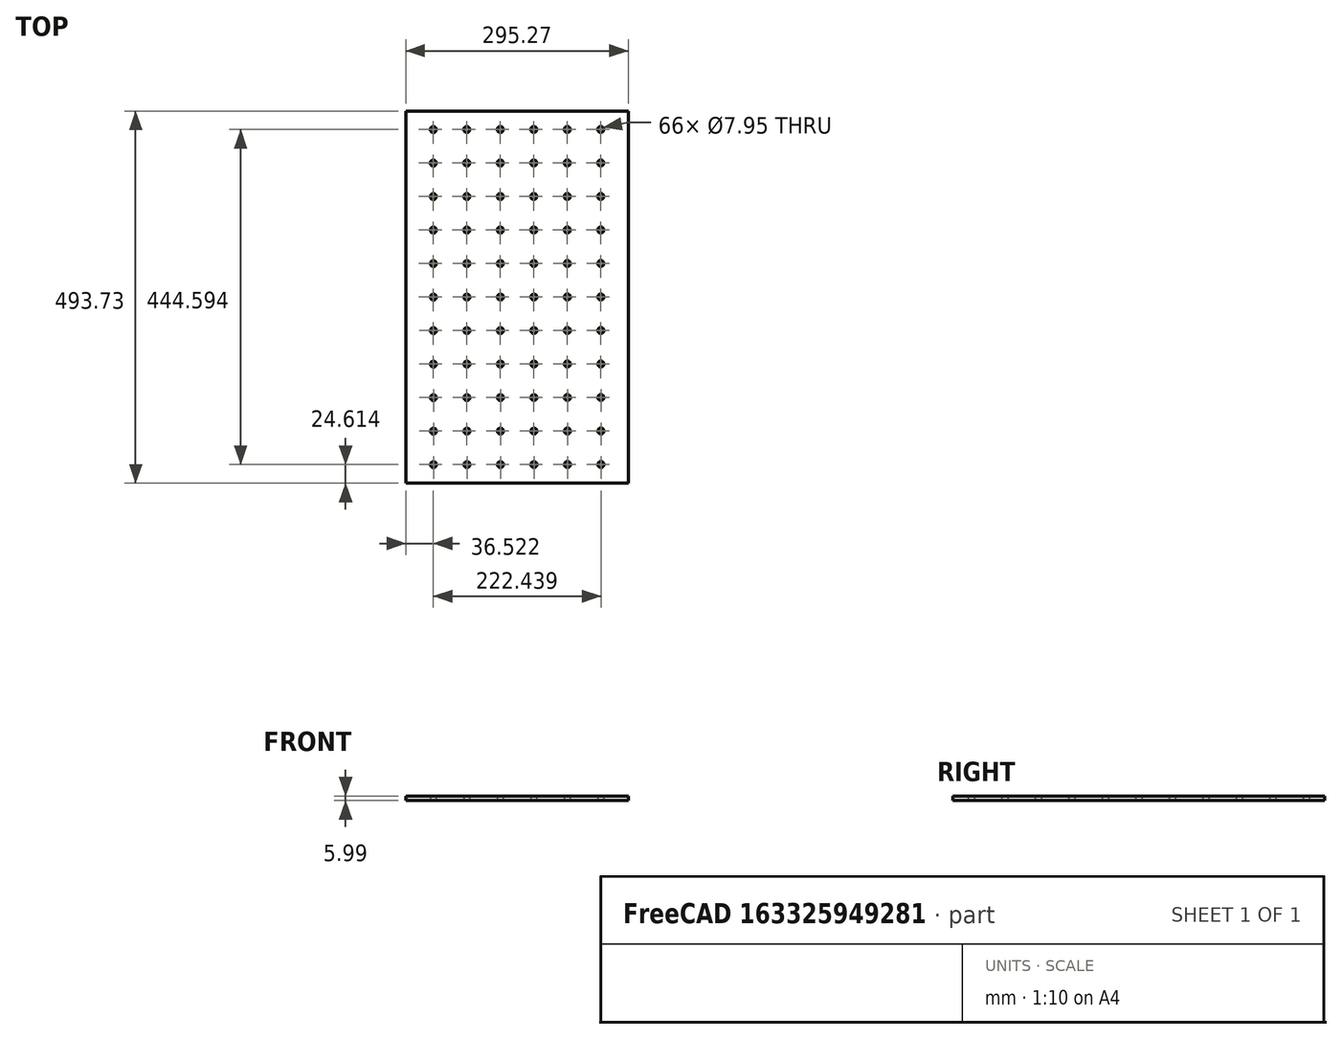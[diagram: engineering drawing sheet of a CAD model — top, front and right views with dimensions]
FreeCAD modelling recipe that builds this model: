
FCSTD DOCUMENT  (FreeCAD 0.19R24267 (Git))
Label: Up1-P2
License: All rights reserved
LicenseURL: http://en.wikipedia.org/wiki/All_rights_reserved
objects: TechDraw::DrawViewDimension×8, TechDraw::DrawViewAnnotation×3, TechDraw::DrawProjGroupItem×2, TechDraw::DrawHatch×2, Sketcher::SketchObject×1, Part::Extrusion×1, TechDraw::DrawSVGTemplate×1, TechDraw::DrawProjGroup×1, TechDraw::DrawPage×1
note: 2 computed .brp shape members not serialized (recipe doc carries the construction recipe); baked Part::Feature solids carry a one-line shape summary decoded from their .brp

FEATURE [Sketcher::SketchObject] Sketch
  FullyConstrained = false
  sketch-geometry (135):
    g0: LineSegment StartX=210.166 StartY=-388.383 StartZ=0 EndX=505.441 EndY=-388.383 EndZ=0
    g1: LineSegment StartX=505.441 StartY=-388.383 StartZ=0 EndX=505.441 EndY=-882.108 EndZ=0
    g2: LineSegment StartX=505.441 StartY=-882.108 StartZ=0 EndX=210.166 EndY=-882.108 EndZ=0
    g3: LineSegment StartX=210.166 StartY=-882.108 StartZ=0 EndX=210.166 EndY=-388.383 EndZ=0
    g4: Circle CenterX=246.692 CenterY=-412.996 CenterZ=0 NormalX=0 NormalY=0 NormalZ=1 AngleXU=0 Radius=3.9751
    g5: Circle CenterX=291.142 CenterY=-412.977 CenterZ=0 NormalX=0 NormalY=0 NormalZ=1 AngleXU=0 Radius=3.9751
    g6: LineSegment StartX=246.692 StartY=-412.996 StartZ=0 EndX=291.142 EndY=-412.977 EndZ=0
    g7: Circle CenterX=335.592 CenterY=-412.958 CenterZ=0 NormalX=0 NormalY=0 NormalZ=1 AngleXU=0 Radius=3.9751
    g8: LineSegment StartX=291.142 StartY=-412.977 StartZ=0 EndX=335.592 EndY=-412.958 EndZ=0
    g9: Circle CenterX=380.042 CenterY=-412.939 CenterZ=0 NormalX=0 NormalY=0 NormalZ=1 AngleXU=0 Radius=3.9751
    g10: LineSegment StartX=335.592 StartY=-412.958 StartZ=0 EndX=380.042 EndY=-412.939 EndZ=0
    g11: Circle CenterX=424.492 CenterY=-412.92 CenterZ=0 NormalX=0 NormalY=0 NormalZ=1 AngleXU=0 Radius=3.9751
    g12: LineSegment StartX=380.042 StartY=-412.939 StartZ=0 EndX=424.492 EndY=-412.92 EndZ=0
    g13: Circle CenterX=468.942 CenterY=-412.901 CenterZ=0 NormalX=0 NormalY=0 NormalZ=1 AngleXU=0 Radius=3.9751
    g14: LineSegment StartX=424.492 StartY=-412.92 StartZ=0 EndX=468.942 EndY=-412.901 EndZ=0
    g15: Circle CenterX=246.71 CenterY=-457.446 CenterZ=0 NormalX=0 NormalY=0 NormalZ=1 AngleXU=0 Radius=3.9751
    g16: LineSegment StartX=246.692 StartY=-412.996 StartZ=0 EndX=246.71 EndY=-457.446 EndZ=0
    g17: Circle CenterX=291.16 CenterY=-457.427 CenterZ=0 NormalX=0 NormalY=0 NormalZ=1 AngleXU=0 Radius=3.9751
    g18: LineSegment StartX=246.71 StartY=-457.446 StartZ=0 EndX=291.16 EndY=-457.427 EndZ=0
    g19: Circle CenterX=335.61 CenterY=-457.408 CenterZ=0 NormalX=0 NormalY=0 NormalZ=1 AngleXU=0 Radius=3.9751
    g20: LineSegment StartX=291.16 StartY=-457.427 StartZ=0 EndX=335.61 EndY=-457.408 EndZ=0
    g21: Circle CenterX=380.06 CenterY=-457.389 CenterZ=0 NormalX=0 NormalY=0 NormalZ=1 AngleXU=0 Radius=3.9751
    g22: LineSegment StartX=335.61 StartY=-457.408 StartZ=0 EndX=380.06 EndY=-457.389 EndZ=0
    g23: Circle CenterX=424.51 CenterY=-457.37 CenterZ=0 NormalX=0 NormalY=0 NormalZ=1 AngleXU=0 Radius=3.9751
    g24: LineSegment StartX=380.06 StartY=-457.389 StartZ=0 EndX=424.51 EndY=-457.37 EndZ=0
    g25: Circle CenterX=468.96 CenterY=-457.351 CenterZ=0 NormalX=0 NormalY=0 NormalZ=1 AngleXU=0 Radius=3.9751
    g26: LineSegment StartX=424.51 StartY=-457.37 StartZ=0 EndX=468.96 EndY=-457.351 EndZ=0
    g27: Circle CenterX=246.729 CenterY=-501.896 CenterZ=0 NormalX=0 NormalY=0 NormalZ=1 AngleXU=0 Radius=3.9751
    g28: LineSegment StartX=246.71 StartY=-457.446 StartZ=0 EndX=246.729 EndY=-501.896 EndZ=0
    g29: Circle CenterX=291.179 CenterY=-501.877 CenterZ=0 NormalX=0 NormalY=0 NormalZ=1 AngleXU=0 Radius=3.9751
    g30: LineSegment StartX=246.729 StartY=-501.896 StartZ=0 EndX=291.179 EndY=-501.877 EndZ=0
    g31: Circle CenterX=335.629 CenterY=-501.858 CenterZ=0 NormalX=0 NormalY=0 NormalZ=1 AngleXU=0 Radius=3.9751
    g32: LineSegment StartX=291.179 StartY=-501.877 StartZ=0 EndX=335.629 EndY=-501.858 EndZ=0
    g33: Circle CenterX=380.079 CenterY=-501.839 CenterZ=0 NormalX=0 NormalY=0 NormalZ=1 AngleXU=0 Radius=3.9751
    g34: LineSegment StartX=335.629 StartY=-501.858 StartZ=0 EndX=380.079 EndY=-501.839 EndZ=0
    g35: Circle CenterX=424.529 CenterY=-501.82 CenterZ=0 NormalX=0 NormalY=0 NormalZ=1 AngleXU=0 Radius=3.9751
    g36: LineSegment StartX=380.079 StartY=-501.839 StartZ=0 EndX=424.529 EndY=-501.82 EndZ=0
    g37: Circle CenterX=468.979 CenterY=-501.801 CenterZ=0 NormalX=0 NormalY=0 NormalZ=1 AngleXU=0 Radius=3.9751
    g38: LineSegment StartX=424.529 StartY=-501.82 StartZ=0 EndX=468.979 EndY=-501.801 EndZ=0
    g39: Circle CenterX=246.748 CenterY=-546.346 CenterZ=0 NormalX=0 NormalY=0 NormalZ=1 AngleXU=0 Radius=3.9751
    g40: LineSegment StartX=246.729 StartY=-501.896 StartZ=0 EndX=246.748 EndY=-546.346 EndZ=0
    g41: Circle CenterX=291.198 CenterY=-546.327 CenterZ=0 NormalX=0 NormalY=0 NormalZ=1 AngleXU=0 Radius=3.9751
    g42: LineSegment StartX=246.748 StartY=-546.346 StartZ=0 EndX=291.198 EndY=-546.327 EndZ=0
    g43: Circle CenterX=335.648 CenterY=-546.308 CenterZ=0 NormalX=0 NormalY=0 NormalZ=1 AngleXU=0 Radius=3.9751
    g44: LineSegment StartX=291.198 StartY=-546.327 StartZ=0 EndX=335.648 EndY=-546.308 EndZ=0
    g45: Circle CenterX=380.098 CenterY=-546.289 CenterZ=0 NormalX=0 NormalY=0 NormalZ=1 AngleXU=0 Radius=3.9751
    g46: LineSegment StartX=335.648 StartY=-546.308 StartZ=0 EndX=380.098 EndY=-546.289 EndZ=0
    g47: Circle CenterX=424.548 CenterY=-546.27 CenterZ=0 NormalX=0 NormalY=0 NormalZ=1 AngleXU=0 Radius=3.9751
    g48: LineSegment StartX=380.098 StartY=-546.289 StartZ=0 EndX=424.548 EndY=-546.27 EndZ=0
    g49: Circle CenterX=468.998 CenterY=-546.251 CenterZ=0 NormalX=0 NormalY=0 NormalZ=1 AngleXU=0 Radius=3.9751
    g50: LineSegment StartX=424.548 StartY=-546.27 StartZ=0 EndX=468.998 EndY=-546.251 EndZ=0
    g51: Circle CenterX=246.767 CenterY=-590.796 CenterZ=0 NormalX=0 NormalY=0 NormalZ=1 AngleXU=0 Radius=3.9751
    g52: LineSegment StartX=246.748 StartY=-546.346 StartZ=0 EndX=246.767 EndY=-590.796 EndZ=0
    g53: Circle CenterX=291.217 CenterY=-590.777 CenterZ=0 NormalX=0 NormalY=0 NormalZ=1 AngleXU=0 Radius=3.9751
    g54: LineSegment StartX=246.767 StartY=-590.796 StartZ=0 EndX=291.217 EndY=-590.777 EndZ=0
    g55: Circle CenterX=335.667 CenterY=-590.758 CenterZ=0 NormalX=0 NormalY=0 NormalZ=1 AngleXU=0 Radius=3.9751
    g56: LineSegment StartX=291.217 StartY=-590.777 StartZ=0 EndX=335.667 EndY=-590.758 EndZ=0
    g57: Circle CenterX=380.117 CenterY=-590.739 CenterZ=0 NormalX=0 NormalY=0 NormalZ=1 AngleXU=0 Radius=3.9751
    g58: LineSegment StartX=335.667 StartY=-590.758 StartZ=0 EndX=380.117 EndY=-590.739 EndZ=0
    g59: Circle CenterX=424.567 CenterY=-590.72 CenterZ=0 NormalX=0 NormalY=0 NormalZ=1 AngleXU=0 Radius=3.9751
    g60: LineSegment StartX=380.117 StartY=-590.739 StartZ=0 EndX=424.567 EndY=-590.72 EndZ=0
    g61: Circle CenterX=469.017 CenterY=-590.701 CenterZ=0 NormalX=0 NormalY=0 NormalZ=1 AngleXU=0 Radius=3.9751
    g62: LineSegment StartX=424.567 StartY=-590.72 StartZ=0 EndX=469.017 EndY=-590.701 EndZ=0
    g63: Circle CenterX=246.786 CenterY=-635.246 CenterZ=0 NormalX=0 NormalY=0 NormalZ=1 AngleXU=0 Radius=3.9751
    g64: LineSegment StartX=246.767 StartY=-590.796 StartZ=0 EndX=246.786 EndY=-635.246 EndZ=0
    g65: Circle CenterX=291.236 CenterY=-635.227 CenterZ=0 NormalX=0 NormalY=0 NormalZ=1 AngleXU=0 Radius=3.9751
    g66: LineSegment StartX=246.786 StartY=-635.246 StartZ=0 EndX=291.236 EndY=-635.227 EndZ=0
    g67: Circle CenterX=335.686 CenterY=-635.208 CenterZ=0 NormalX=0 NormalY=0 NormalZ=1 AngleXU=0 Radius=3.9751
    g68: LineSegment StartX=291.236 StartY=-635.227 StartZ=0 EndX=335.686 EndY=-635.208 EndZ=0
    g69: Circle CenterX=380.136 CenterY=-635.189 CenterZ=0 NormalX=0 NormalY=0 NormalZ=1 AngleXU=0 Radius=3.9751
    g70: LineSegment StartX=335.686 StartY=-635.208 StartZ=0 EndX=380.136 EndY=-635.189 EndZ=0
    g71: Circle CenterX=424.586 CenterY=-635.17 CenterZ=0 NormalX=0 NormalY=0 NormalZ=1 AngleXU=0 Radius=3.9751
    g72: LineSegment StartX=380.136 StartY=-635.189 StartZ=0 EndX=424.586 EndY=-635.17 EndZ=0
    g73: Circle CenterX=469.036 CenterY=-635.151 CenterZ=0 NormalX=0 NormalY=0 NormalZ=1 AngleXU=0 Radius=3.9751
    g74: LineSegment StartX=424.586 StartY=-635.17 StartZ=0 EndX=469.036 EndY=-635.151 EndZ=0
    g75: Circle CenterX=246.805 CenterY=-679.696 CenterZ=0 NormalX=0 NormalY=0 NormalZ=1 AngleXU=0 Radius=3.9751
    g76: LineSegment StartX=246.786 StartY=-635.246 StartZ=0 EndX=246.805 EndY=-679.696 EndZ=0
    g77: Circle CenterX=291.255 CenterY=-679.677 CenterZ=0 NormalX=0 NormalY=0 NormalZ=1 AngleXU=0 Radius=3.9751
    g78: LineSegment StartX=246.805 StartY=-679.696 StartZ=0 EndX=291.255 EndY=-679.677 EndZ=0
    g79: Circle CenterX=335.705 CenterY=-679.658 CenterZ=0 NormalX=0 NormalY=0 NormalZ=1 AngleXU=0 Radius=3.9751
    g80: LineSegment StartX=291.255 StartY=-679.677 StartZ=0 EndX=335.705 EndY=-679.658 EndZ=0
    g81: Circle CenterX=380.155 CenterY=-679.639 CenterZ=0 NormalX=0 NormalY=0 NormalZ=1 AngleXU=0 Radius=3.9751
    g82: LineSegment StartX=335.705 StartY=-679.658 StartZ=0 EndX=380.155 EndY=-679.639 EndZ=0
    g83: Circle CenterX=424.605 CenterY=-679.62 CenterZ=0 NormalX=0 NormalY=0 NormalZ=1 AngleXU=0 Radius=3.9751
    g84: LineSegment StartX=380.155 StartY=-679.639 StartZ=0 EndX=424.605 EndY=-679.62 EndZ=0
    g85: Circle CenterX=469.055 CenterY=-679.601 CenterZ=0 NormalX=0 NormalY=0 NormalZ=1 AngleXU=0 Radius=3.9751
    g86: LineSegment StartX=424.605 StartY=-679.62 StartZ=0 EndX=469.055 EndY=-679.601 EndZ=0
    g87: Circle CenterX=246.824 CenterY=-724.146 CenterZ=0 NormalX=0 NormalY=0 NormalZ=1 AngleXU=0 Radius=3.9751
    g88: LineSegment StartX=246.805 StartY=-679.696 StartZ=0 EndX=246.824 EndY=-724.146 EndZ=0
    g89: Circle CenterX=291.274 CenterY=-724.127 CenterZ=0 NormalX=0 NormalY=0 NormalZ=1 AngleXU=0 Radius=3.9751
    g90: LineSegment StartX=246.824 StartY=-724.146 StartZ=0 EndX=291.274 EndY=-724.127 EndZ=0
    g91: Circle CenterX=335.724 CenterY=-724.108 CenterZ=0 NormalX=0 NormalY=0 NormalZ=1 AngleXU=0 Radius=3.9751
    g92: LineSegment StartX=291.274 StartY=-724.127 StartZ=0 EndX=335.724 EndY=-724.108 EndZ=0
    g93: Circle CenterX=380.174 CenterY=-724.089 CenterZ=0 NormalX=0 NormalY=0 NormalZ=1 AngleXU=0 Radius=3.9751
    g94: LineSegment StartX=335.724 StartY=-724.108 StartZ=0 EndX=380.174 EndY=-724.089 EndZ=0
    g95: Circle CenterX=424.624 CenterY=-724.07 CenterZ=0 NormalX=0 NormalY=0 NormalZ=1 AngleXU=0 Radius=3.9751
    g96: LineSegment StartX=380.174 StartY=-724.089 StartZ=0 EndX=424.624 EndY=-724.07 EndZ=0
    g97: Circle CenterX=469.074 CenterY=-724.051 CenterZ=0 NormalX=0 NormalY=0 NormalZ=1 AngleXU=0 Radius=3.9751
    g98: LineSegment StartX=424.624 StartY=-724.07 StartZ=0 EndX=469.074 EndY=-724.051 EndZ=0
    g99: Circle CenterX=246.843 CenterY=-768.596 CenterZ=0 NormalX=0 NormalY=0 NormalZ=1 AngleXU=0 Radius=3.9751
    g100: LineSegment StartX=246.824 StartY=-724.146 StartZ=0 EndX=246.843 EndY=-768.596 EndZ=0
    g101: Circle CenterX=291.293 CenterY=-768.577 CenterZ=0 NormalX=0 NormalY=0 NormalZ=1 AngleXU=0 Radius=3.9751
    g102: LineSegment StartX=246.843 StartY=-768.596 StartZ=0 EndX=291.293 EndY=-768.577 EndZ=0
    g103: Circle CenterX=335.743 CenterY=-768.558 CenterZ=0 NormalX=0 NormalY=0 NormalZ=1 AngleXU=0 Radius=3.9751
    g104: LineSegment StartX=291.293 StartY=-768.577 StartZ=0 EndX=335.743 EndY=-768.558 EndZ=0
    g105: Circle CenterX=380.193 CenterY=-768.539 CenterZ=0 NormalX=0 NormalY=0 NormalZ=1 AngleXU=0 Radius=3.9751
    g106: LineSegment StartX=335.743 StartY=-768.558 StartZ=0 EndX=380.193 EndY=-768.539 EndZ=0
    g107: Circle CenterX=424.643 CenterY=-768.52 CenterZ=0 NormalX=0 NormalY=0 NormalZ=1 AngleXU=0 Radius=3.9751
    g108: LineSegment StartX=380.193 StartY=-768.539 StartZ=0 EndX=424.643 EndY=-768.52 EndZ=0
    g109: Circle CenterX=469.093 CenterY=-768.501 CenterZ=0 NormalX=0 NormalY=0 NormalZ=1 AngleXU=0 Radius=3.9751
    g110: LineSegment StartX=424.643 StartY=-768.52 StartZ=0 EndX=469.093 EndY=-768.501 EndZ=0
    g111: Circle CenterX=246.862 CenterY=-813.046 CenterZ=0 NormalX=0 NormalY=0 NormalZ=1 AngleXU=0 Radius=3.9751
    g112: LineSegment StartX=246.843 StartY=-768.596 StartZ=0 EndX=246.862 EndY=-813.046 EndZ=0
    g113: Circle CenterX=291.312 CenterY=-813.027 CenterZ=0 NormalX=0 NormalY=0 NormalZ=1 AngleXU=0 Radius=3.9751
    g114: LineSegment StartX=246.862 StartY=-813.046 StartZ=0 EndX=291.312 EndY=-813.027 EndZ=0
    g115: Circle CenterX=335.762 CenterY=-813.008 CenterZ=0 NormalX=0 NormalY=0 NormalZ=1 AngleXU=0 Radius=3.9751
    g116: LineSegment StartX=291.312 StartY=-813.027 StartZ=0 EndX=335.762 EndY=-813.008 EndZ=0
    g117: Circle CenterX=380.212 CenterY=-812.989 CenterZ=0 NormalX=0 NormalY=0 NormalZ=1 AngleXU=0 Radius=3.9751
    g118: LineSegment StartX=335.762 StartY=-813.008 StartZ=0 EndX=380.212 EndY=-812.989 EndZ=0
    g119: Circle CenterX=424.662 CenterY=-812.97 CenterZ=0 NormalX=0 NormalY=0 NormalZ=1 AngleXU=0 Radius=3.9751
    g120: LineSegment StartX=380.212 StartY=-812.989 StartZ=0 EndX=424.662 EndY=-812.97 EndZ=0
    g121: Circle CenterX=469.112 CenterY=-812.951 CenterZ=0 NormalX=0 NormalY=0 NormalZ=1 AngleXU=0 Radius=3.9751
    g122: LineSegment StartX=424.662 StartY=-812.97 StartZ=0 EndX=469.112 EndY=-812.951 EndZ=0
    g123: Circle CenterX=246.88 CenterY=-857.496 CenterZ=0 NormalX=0 NormalY=0 NormalZ=1 AngleXU=0 Radius=3.9751
    g124: LineSegment StartX=246.862 StartY=-813.046 StartZ=0 EndX=246.88 EndY=-857.496 EndZ=0
    g125: Circle CenterX=291.33 CenterY=-857.477 CenterZ=0 NormalX=0 NormalY=0 NormalZ=1 AngleXU=0 Radius=3.9751
    g126: LineSegment StartX=246.88 StartY=-857.496 StartZ=0 EndX=291.33 EndY=-857.477 EndZ=0
    g127: Circle CenterX=335.78 CenterY=-857.458 CenterZ=0 NormalX=0 NormalY=0 NormalZ=1 AngleXU=0 Radius=3.9751
    g128: LineSegment StartX=291.33 StartY=-857.477 StartZ=0 EndX=335.78 EndY=-857.458 EndZ=0
    g129: Circle CenterX=380.23 CenterY=-857.439 CenterZ=0 NormalX=0 NormalY=0 NormalZ=1 AngleXU=0 Radius=3.9751
    g130: LineSegment StartX=335.78 StartY=-857.458 StartZ=0 EndX=380.23 EndY=-857.439 EndZ=0
    g131: Circle CenterX=424.68 CenterY=-857.42 CenterZ=0 NormalX=0 NormalY=0 NormalZ=1 AngleXU=0 Radius=3.9751
    g132: LineSegment StartX=380.23 StartY=-857.439 StartZ=0 EndX=424.68 EndY=-857.42 EndZ=0
    g133: Circle CenterX=469.13 CenterY=-857.401 CenterZ=0 NormalX=0 NormalY=0 NormalZ=1 AngleXU=0 Radius=3.9751
    g134: LineSegment StartX=424.68 StartY=-857.42 StartZ=0 EndX=469.13 EndY=-857.401 EndZ=0
  constraints (338):
    c: Coincident(g0,g1)
    c: Coincident(g1,g2)
    c: Coincident(g2,g3)
    c: Coincident(g3,g0)
    c: Horizontal(g0)
    c: Horizontal(g2)
    c: Vertical(g1)
    c: Vertical(g3)
    c: Distance(g0,g1) = 295.275
    c: Distance(g0,g2) = 493.725
    c: Diameter(g4) = 7.9502
    c: Distance(g4,g3) = 36.5252
    c: Distance(g4,g0) = 24.6126
    c: Diameter(g5) = 7.9502
    c: Coincident(g4,g6)
    c: Coincident(g5,g6)
    c: Distance(g6) = 44.45
    c: Angle(g6) = 0.00042473
    c: Diameter(g7) = 7.9502
    c: Coincident(g5,g8)
    c: Coincident(g7,g8)
    c: Equal(g6,g8)
    c: Parallel(g8,g6)
    c: Diameter(g9) = 7.9502
    c: Coincident(g7,g10)
    c: Coincident(g9,g10)
    c: Equal(g6,g10)
    c: Parallel(g10,g6)
    c: Diameter(g11) = 7.9502
    c: Coincident(g9,g12)
    c: Coincident(g11,g12)
    c: Equal(g6,g12)
    c: Parallel(g12,g6)
    c: Diameter(g13) = 7.9502
    c: Coincident(g11,g14)
    c: Coincident(g13,g14)
    c: Equal(g6,g14)
    c: Parallel(g14,g6)
    c: Diameter(g15) = 7.9502
    c: Coincident(g4,g16)
    c: Coincident(g15,g16)
    c: Equal(g16,g6)
    c: Perpendicular(g16,g6)
    c: Diameter(g17) = 7.9502
    c: Coincident(g15,g18)
    c: Coincident(g17,g18)
    c: Equal(g6,g18)
    c: Parallel(g18,g6)
    c: Diameter(g19) = 7.9502
    c: Coincident(g17,g20)
    c: Coincident(g19,g20)
    c: Equal(g6,g20)
    c: Parallel(g20,g6)
    c: Diameter(g21) = 7.9502
    c: Coincident(g19,g22)
    c: Coincident(g21,g22)
    c: Equal(g6,g22)
    c: Parallel(g22,g6)
    c: Diameter(g23) = 7.9502
    c: Coincident(g21,g24)
    c: Coincident(g23,g24)
    c: Equal(g6,g24)
    c: Parallel(g24,g6)
    c: Diameter(g25) = 7.9502
    c: Coincident(g23,g26)
    c: Coincident(g25,g26)
    c: Equal(g6,g26)
    c: Parallel(g26,g6)
    c: Diameter(g27) = 7.9502
    c: Coincident(g15,g28)
    c: Coincident(g27,g28)
    c: Equal(g16,g28)
    c: Perpendicular(g28,g6)
    c: Diameter(g29) = 7.9502
    c: Coincident(g27,g30)
    c: Coincident(g29,g30)
    c: Equal(g6,g30)
    c: Parallel(g30,g6)
    c: Diameter(g31) = 7.9502
    c: Coincident(g29,g32)
    c: Coincident(g31,g32)
    c: Equal(g6,g32)
    c: Parallel(g32,g6)
    c: Diameter(g33) = 7.9502
    c: Coincident(g31,g34)
    c: Coincident(g33,g34)
    c: Equal(g6,g34)
    c: Parallel(g34,g6)
    c: Diameter(g35) = 7.9502
    c: Coincident(g33,g36)
    c: Coincident(g35,g36)
    c: Equal(g6,g36)
    c: Parallel(g36,g6)
    c: Diameter(g37) = 7.9502
    c: Coincident(g35,g38)
    c: Coincident(g37,g38)
    c: Equal(g6,g38)
    c: Parallel(g38,g6)
    c: Diameter(g39) = 7.9502
    c: Coincident(g27,g40)
    c: Coincident(g39,g40)
    c: Equal(g16,g40)
    c: Perpendicular(g40,g6)
    c: Diameter(g41) = 7.9502
    c: Coincident(g39,g42)
    c: Coincident(g41,g42)
    c: Equal(g6,g42)
    c: Parallel(g42,g6)
    c: Diameter(g43) = 7.9502
    c: Coincident(g41,g44)
    c: Coincident(g43,g44)
    c: Equal(g6,g44)
    c: Parallel(g44,g6)
    c: Diameter(g45) = 7.9502
    c: Coincident(g43,g46)
    c: Coincident(g45,g46)
    c: Equal(g6,g46)
    c: Parallel(g46,g6)
    c: Diameter(g47) = 7.9502
    c: Coincident(g45,g48)
    c: Coincident(g47,g48)
    c: Equal(g6,g48)
    c: Parallel(g48,g6)
    c: Diameter(g49) = 7.9502
    c: Coincident(g47,g50)
    c: Coincident(g49,g50)
    c: Equal(g6,g50)
    c: Parallel(g50,g6)
    c: Diameter(g51) = 7.9502
    c: Coincident(g39,g52)
    c: Coincident(g51,g52)
    c: Equal(g16,g52)
    c: Perpendicular(g52,g6)
    c: Diameter(g53) = 7.9502
    c: Coincident(g51,g54)
    c: Coincident(g53,g54)
    c: Equal(g6,g54)
    c: Parallel(g54,g6)
    c: Diameter(g55) = 7.9502
    c: Coincident(g53,g56)
    c: Coincident(g55,g56)
    c: Equal(g6,g56)
    c: Parallel(g56,g6)
    c: Diameter(g57) = 7.9502
    c: Coincident(g55,g58)
    c: Coincident(g57,g58)
    c: Equal(g6,g58)
    c: Parallel(g58,g6)
    c: Diameter(g59) = 7.9502
    c: Coincident(g57,g60)
    c: Coincident(g59,g60)
    c: Equal(g6,g60)
    c: Parallel(g60,g6)
    c: Diameter(g61) = 7.9502
    c: Coincident(g59,g62)
    c: Coincident(g61,g62)
    c: Equal(g6,g62)
    c: Parallel(g62,g6)
    c: Diameter(g63) = 7.9502
    c: Coincident(g51,g64)
    c: Coincident(g63,g64)
    c: Equal(g16,g64)
    c: Perpendicular(g64,g6)
    c: Diameter(g65) = 7.9502
    c: Coincident(g63,g66)
    c: Coincident(g65,g66)
    c: Equal(g6,g66)
    c: Parallel(g66,g6)
    c: Diameter(g67) = 7.9502
    c: Coincident(g65,g68)
    c: Coincident(g67,g68)
    c: Equal(g6,g68)
    c: Parallel(g68,g6)
    c: Diameter(g69) = 7.9502
    c: Coincident(g67,g70)
    c: Coincident(g69,g70)
    c: Equal(g6,g70)
    c: Parallel(g70,g6)
    c: Diameter(g71) = 7.9502
    c: Coincident(g69,g72)
    c: Coincident(g71,g72)
    c: Equal(g6,g72)
    c: Parallel(g72,g6)
    c: Diameter(g73) = 7.9502
    c: Coincident(g71,g74)
    c: Coincident(g73,g74)
    c: Equal(g6,g74)
    c: Parallel(g74,g6)
    c: Diameter(g75) = 7.9502
    c: Coincident(g63,g76)
    c: Coincident(g75,g76)
    c: Equal(g16,g76)
    c: Perpendicular(g76,g6)
    c: Diameter(g77) = 7.9502
    c: Coincident(g75,g78)
    c: Coincident(g77,g78)
    c: Equal(g6,g78)
    c: Parallel(g78,g6)
    c: Diameter(g79) = 7.9502
    c: Coincident(g77,g80)
    c: Coincident(g79,g80)
    c: Equal(g6,g80)
    c: Parallel(g80,g6)
    c: Diameter(g81) = 7.9502
    c: Coincident(g79,g82)
    c: Coincident(g81,g82)
    c: Equal(g6,g82)
    c: Parallel(g82,g6)
    c: Diameter(g83) = 7.9502
    c: Coincident(g81,g84)
    c: Coincident(g83,g84)
    c: Equal(g6,g84)
    c: Parallel(g84,g6)
    c: Diameter(g85) = 7.9502
    c: Coincident(g83,g86)
    c: Coincident(g85,g86)
    c: Equal(g6,g86)
    c: Parallel(g86,g6)
    c: Diameter(g87) = 7.9502
    c: Coincident(g75,g88)
    c: Coincident(g87,g88)
    c: Equal(g16,g88)
    c: Perpendicular(g88,g6)
    c: Diameter(g89) = 7.9502
    c: Coincident(g87,g90)
    c: Coincident(g89,g90)
    c: Equal(g6,g90)
    c: Parallel(g90,g6)
    c: Diameter(g91) = 7.9502
    c: Coincident(g89,g92)
    c: Coincident(g91,g92)
    c: Equal(g6,g92)
    c: Parallel(g92,g6)
    c: Diameter(g93) = 7.9502
    c: Coincident(g91,g94)
    c: Coincident(g93,g94)
    c: Equal(g6,g94)
    c: Parallel(g94,g6)
    c: Diameter(g95) = 7.9502
    c: Coincident(g93,g96)
    c: Coincident(g95,g96)
    c: Equal(g6,g96)
    c: Parallel(g96,g6)
    c: Diameter(g97) = 7.9502
    c: Coincident(g95,g98)
    c: Coincident(g97,g98)
    c: Equal(g6,g98)
    c: Parallel(g98,g6)
    c: Diameter(g99) = 7.9502
    c: Coincident(g87,g100)
    c: Coincident(g99,g100)
    c: Equal(g16,g100)
    c: Perpendicular(g100,g6)
    c: Diameter(g101) = 7.9502
    c: Coincident(g99,g102)
    c: Coincident(g101,g102)
    c: Equal(g6,g102)
    c: Parallel(g102,g6)
    c: Diameter(g103) = 7.9502
    c: Coincident(g101,g104)
    c: Coincident(g103,g104)
    c: Equal(g6,g104)
    c: Parallel(g104,g6)
    c: Diameter(g105) = 7.9502
    c: Coincident(g103,g106)
    c: Coincident(g105,g106)
    c: Equal(g6,g106)
    c: Parallel(g106,g6)
    c: Diameter(g107) = 7.9502
    c: Coincident(g105,g108)
    c: Coincident(g107,g108)
    c: Equal(g6,g108)
    c: Parallel(g108,g6)
    c: Diameter(g109) = 7.9502
    c: Coincident(g107,g110)
    c: Coincident(g109,g110)
    c: Equal(g6,g110)
    c: Parallel(g110,g6)
    c: Diameter(g111) = 7.9502
    c: Coincident(g99,g112)
    c: Coincident(g111,g112)
    c: Equal(g16,g112)
    c: Perpendicular(g112,g6)
    c: Diameter(g113) = 7.9502
    c: Coincident(g111,g114)
    c: Coincident(g113,g114)
    c: Equal(g6,g114)
    c: Parallel(g114,g6)
    c: Diameter(g115) = 7.9502
    c: Coincident(g113,g116)
    c: Coincident(g115,g116)
    c: Equal(g6,g116)
    c: Parallel(g116,g6)
    c: Diameter(g117) = 7.9502
    c: Coincident(g115,g118)
    c: Coincident(g117,g118)
    c: Equal(g6,g118)
    c: Parallel(g118,g6)
    c: Diameter(g119) = 7.9502
    c: Coincident(g117,g120)
    c: Coincident(g119,g120)
    c: Equal(g6,g120)
    c: Parallel(g120,g6)
    c: Diameter(g121) = 7.9502
    c: Coincident(g119,g122)
    c: Coincident(g121,g122)
    c: Equal(g6,g122)
    c: Parallel(g122,g6)
    c: Diameter(g123) = 7.9502
    c: Coincident(g111,g124)
    c: Coincident(g123,g124)
    c: Equal(g16,g124)
    c: Perpendicular(g124,g6)
    c: Diameter(g125) = 7.9502
    c: Coincident(g123,g126)
    c: Coincident(g125,g126)
    c: Equal(g6,g126)
    c: Parallel(g126,g6)
    c: Diameter(g127) = 7.9502
    c: Coincident(g125,g128)
    c: Coincident(g127,g128)
    c: Equal(g6,g128)
    c: Parallel(g128,g6)
    c: Diameter(g129) = 7.9502
    c: Coincident(g127,g130)
    c: Coincident(g129,g130)
    c: Equal(g6,g130)
    c: Parallel(g130,g6)
    c: Diameter(g131) = 7.9502
    c: Coincident(g129,g132)
    c: Coincident(g131,g132)
    c: Equal(g6,g132)
    c: Parallel(g132,g6)
    c: Diameter(g133) = 7.9502
    c: Coincident(g131,g134)
    c: Coincident(g133,g134)
    c: Equal(g6,g134)
    c: Parallel(g134,g6)
FEATURE [Part::Extrusion] Extrude
  Base = -> Sketch
  Dir = (0,0,1)
  DirMode = 2
  FaceMakerClass = Part::FaceMakerBullseye
  LengthFwd = 5.9944
  LengthRev = 0
  Solid = true
  Symmetric = false
FEATURE [TechDraw::DrawSVGTemplate] Template
  Height = 215.9
  Orientation = 1
  Width = 279.4
FEATURE [TechDraw::DrawProjGroupItem] ProjItem  label="Front"
  CoarseView = false
  Direction = (0,0,1)
  Focus = 100
  HardHidden = false
  IsoCount = 0
  IsoHidden = false
  IsoVisible = false
  LockPosition = true
  Perspective = false
  Rotation = 0
  RotationVector = (1,0,0)
  Scale = 0.25
  ScaleType = 2
  SeamHidden = false
  SeamVisible = true
  SmoothHidden = false
  SmoothVisible = true
  Source = -> [Extrude]
  Type = 0
  X = 0
  XDirection = (1,0,0)
  Y = 0
FEATURE [TechDraw::DrawProjGroupItem] ProjItem001  label="Left"
  CoarseView = false
  Direction = (-1,0,1e-16)
  Focus = 100
  HardHidden = false
  IsoCount = 0
  IsoHidden = false
  IsoVisible = false
  LockPosition = false
  Perspective = false
  Rotation = 0
  RotationVector = (1,0,0)
  ScaleType = 2
  SeamHidden = false
  SeamVisible = true
  SmoothHidden = false
  SmoothVisible = true
  Source = -> [Extrude]
  Type = 1
  X = 66.7324
  XDirection = (1e-16,0,1)
  Y = 0
FEATURE [TechDraw::DrawProjGroup] ProjGroup
  Anchor = -> ProjItem
  AutoDistribute = true
  LockPosition = false
  ProjectionType = 0
  Rotation = 0
  Scale = 0.25
  ScaleType = 2
  Source = -> [Extrude]
  Views = -> [ProjItem,ProjItem001]
  X = 139.7
  Y = 107.95
  spacingX = 15.0114
  spacingY = 15.0114
FEATURE [TechDraw::DrawViewDimension] Dimension
  Arbitrary = false
  ArbitraryTolerances = false
  EqualTolerance = true
  FormatSpec = %.3f
  FormatSpecOverTolerance = %+.3f
  FormatSpecUnderTolerance = %+.3f
  Inverted = false
  LockPosition = false
  MeasureType = 1
  OverTolerance = 0
  References2D = -> [ProjItem]
  Rotation = 0
  ScaleType = 0
  TheoreticalExact = false
  Type = 1
  UnderTolerance = 0
  X = 0.690935
  Y = -67.2471
FEATURE [TechDraw::DrawViewDimension] Dimension001
  Arbitrary = false
  ArbitraryTolerances = false
  EqualTolerance = true
  FormatSpec = %.3f
  FormatSpecOverTolerance = %+.3f
  FormatSpecUnderTolerance = %+.3f
  Inverted = false
  LockPosition = false
  MeasureType = 1
  OverTolerance = 0
  References2D = -> [ProjItem001]
  Rotation = 0
  ScaleType = 0
  TheoreticalExact = false
  Type = 1
  UnderTolerance = 0
  X = 13.2414
  Y = 44.2657
FEATURE [TechDraw::DrawViewDimension] Dimension002
  Arbitrary = false
  ArbitraryTolerances = false
  EqualTolerance = true
  FormatSpec = %.3f
  FormatSpecOverTolerance = %+.3f
  FormatSpecUnderTolerance = %+.3f
  Inverted = false
  LockPosition = false
  MeasureType = 1
  OverTolerance = 0
  References2D = -> [ProjItem]
  Rotation = 0
  ScaleType = 0
  TheoreticalExact = false
  Type = 2
  UnderTolerance = 0
  X = 44.1841
  Y = 0.559594
FEATURE [TechDraw::DrawViewDimension] Dimension003
  Arbitrary = false
  ArbitraryTolerances = false
  EqualTolerance = true
  FormatSpec = %.3f
  FormatSpecOverTolerance = %+.3f
  FormatSpecUnderTolerance = %+.3f
  Inverted = false
  LockPosition = false
  MeasureType = 1
  OverTolerance = 0
  References2D = -> [ProjItem]
  Rotation = 0
  ScaleType = 0
  TheoreticalExact = false
  Type = 1
  UnderTolerance = 0
  X = -48.1843
  Y = 54.6287
FEATURE [TechDraw::DrawViewDimension] Dimension004
  Arbitrary = false
  ArbitraryTolerances = false
  EqualTolerance = true
  FormatSpec = %.3f
  FormatSpecOverTolerance = %+.3f
  FormatSpecUnderTolerance = %+.3f
  Inverted = false
  LockPosition = false
  MeasureType = 1
  OverTolerance = 0
  References2D = -> [ProjItem]
  Rotation = 0
  ScaleType = 0
  TheoreticalExact = false
  Type = 2
  UnderTolerance = 0
  X = -24.4818
  Y = 75.1863
FEATURE [TechDraw::DrawViewDimension] Dimension005
  Arbitrary = false
  ArbitraryTolerances = false
  EqualTolerance = true
  FormatSpec = %.3f
  FormatSpecOverTolerance = %+.3f
  FormatSpecUnderTolerance = %+.3f
  Inverted = false
  LockPosition = false
  MeasureType = 1
  OverTolerance = 0
  References2D = -> [ProjItem]
  Rotation = 0
  ScaleType = 0
  TheoreticalExact = false
  Type = 1
  UnderTolerance = 0
  X = -5.32916
  Y = 20.3392
FEATURE [TechDraw::DrawViewDimension] Dimension006
  Arbitrary = false
  ArbitraryTolerances = false
  EqualTolerance = true
  FormatSpec = %.3f
  FormatSpecOverTolerance = %+.3f
  FormatSpecUnderTolerance = %+.3f
  Inverted = false
  LockPosition = false
  MeasureType = 1
  OverTolerance = 0
  References2D = -> [ProjItem]
  Rotation = 0
  ScaleType = 0
  TheoreticalExact = false
  Type = 2
  UnderTolerance = 0
  X = -0.913583
  Y = 35.4
FEATURE [TechDraw::DrawViewDimension] Dimension007
  Arbitrary = false
  ArbitraryTolerances = false
  EqualTolerance = true
  FormatSpec = ⌀%.3f
  FormatSpecOverTolerance = %+.3f
  FormatSpecUnderTolerance = %+.3f
  Inverted = false
  LockPosition = false
  MeasureType = 1
  OverTolerance = 0
  References2D = -> [ProjItem]
  Rotation = 0
  ScaleType = 0
  TheoreticalExact = false
  Type = 5
  UnderTolerance = 0
  X = -43.8348
  Y = 75.0788
FEATURE [TechDraw::DrawViewAnnotation] Annotation
  Font = osifont
  LineSpace = 80
  LockPosition = false
  MaxWidth = -1
  Rotation = 0
  ScaleType = 0
  Text = Figure S3 (Upright) | Panel 2 [left side interior baffle] | Quantity: 1
  TextSize = 5.0038
  TextStyle = 0
  X = 45.1481
  Y = 195.58
FEATURE [TechDraw::DrawViewAnnotation] Annotation001
  Font = osifont
  LineSpace = 80
  LockPosition = false
  MaxWidth = -1
  Rotation = 0
  ScaleType = 0
  Text = Repeat holes with same spacing and diameter
  TextSize = 5.0038
  TextStyle = 0
  X = 172.335
  Y = 177.653
FEATURE [TechDraw::DrawViewAnnotation] Annotation002
  Font = osifont
  LineSpace = 80
  LockPosition = false
  MaxWidth = -1
  Rotation = 0
  ScaleType = 0
  Text = Units: Inches
  TextSize = 5.0038
  TextStyle = 0
  X = 259.08
  Y = 5.08
FEATURE [TechDraw::DrawPage] Page
  KeepUpdated = true
  NextBalloonIndex = 1
  ProjectionType = 0
  Template = -> Template
  Views = -> [ProjGroup,Dimension,Dimension001,Dimension002,Dimension003,Dimension004,Dimension005,Dimension006,Dimension007,Annotation,Annotation001,Annotation002]
FEATURE [TechDraw::DrawHatch] Hatch  label="HatchF0"
  HatchPattern = <path>
  Source = -> ProjItem [Face0]
FEATURE [TechDraw::DrawHatch] Hatch001  label="Hatch001F0"
  HatchPattern = <path>
  Source = -> ProjItem001 [Face0]
note: 2 file-system paths scrubbed to <path> (originals preserved in the JSON sidecar)
